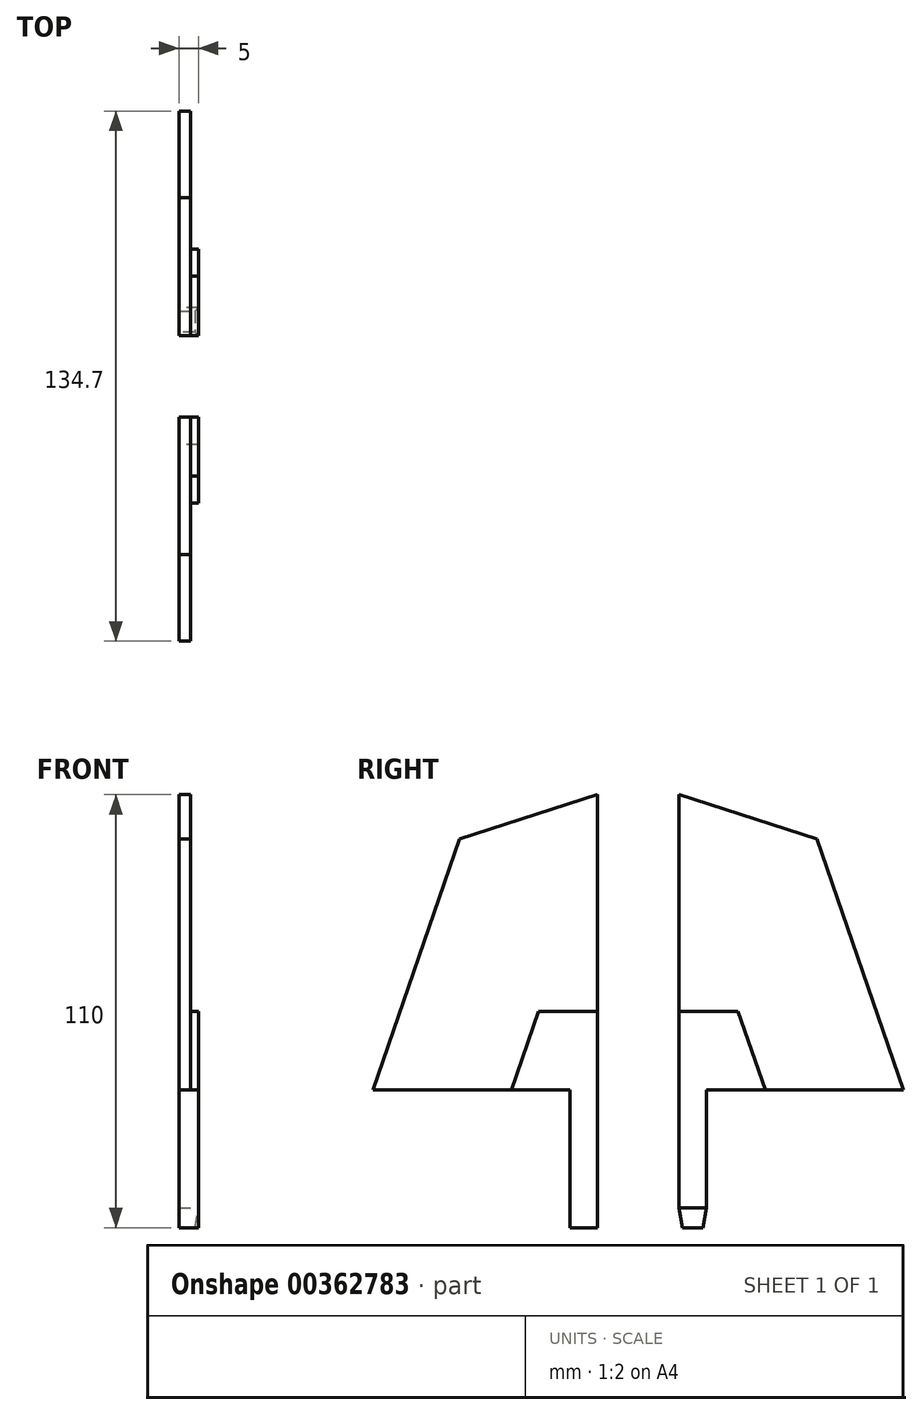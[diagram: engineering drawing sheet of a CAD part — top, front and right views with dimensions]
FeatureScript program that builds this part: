
annotation { "Feature Type Name" : "Feature", "Feature Type Description" : "" }
export const myFeature = defineFeature(function(context is Context, id is Id, definition is map)
    precondition{}
    {
        {
            var Q0;
            Q0=qCreatedBy(makeId("Right.planeOp"),FACE);
            var sketch = newSketch(context, id + "F0", { "sketchPlane" : qUnion([Q0])});
            skLineSegment(sketch, "E0", {"start": v(-17.35, -44.8) * mm, "end": v(-10.35, -44.8) * mm});
            skLineSegment(sketch, "E1", {"start": v(-10.35, -44.8) * mm, "end": v(-10.35, 65.2) * mm});
            skLineSegment(sketch, "E2", {"start": v(-17.35, -44.8) * mm, "end": v(-17.35, -9.8) * mm});
            skLineSegment(sketch, "E3", {"start": v(-17.35, -9.8) * mm, "end": v(-67.35, -9.8) * mm});
            skLineSegment(sketch, "E4", {"start": v(-10.35, 65.2) * mm, "end": v(-45.35, 53.94) * mm});
            skLineSegment(sketch, "E5", {"start": v(-45.35, 53.94) * mm, "end": v(-67.35, -9.8) * mm});
            skLineSegment(sketch, "E6.MirrorCS", {"start": v(10.35, -44.8) * mm, "end": v(10.35, 65.2) * mm});
            skLineSegment(sketch, "E7.MirrorCS", {"start": v(17.35, -44.8) * mm, "end": v(10.35, -44.8) * mm});
            skLineSegment(sketch, "E8.MirrorCS", {"start": v(17.35, -44.8) * mm, "end": v(17.35, -9.8) * mm});
            skLineSegment(sketch, "E9.MirrorCS", {"start": v(17.35, -9.8) * mm, "end": v(67.35, -9.8) * mm});
            skLineSegment(sketch, "E10.MirrorCS", {"start": v(45.35, 53.94) * mm, "end": v(67.35, -9.8) * mm});
            skLineSegment(sketch, "E11.MirrorCS", {"start": v(10.35, 65.2) * mm, "end": v(45.35, 53.94) * mm});
            skLineSegment(sketch, "E12", {"start": v(-10.35, 10.2) * mm, "end": v(-25.35, 10.2) * mm});
            skLineSegment(sketch, "E13", {"start": v(-25.35, 10.2) * mm, "end": v(-32.26, -9.8) * mm});
            skLineSegment(sketch, "E14.MirrorCS", {"start": v(10.35, 10.2) * mm, "end": v(25.35, 10.2) * mm});
            skLineSegment(sketch, "E15.MirrorCS", {"start": v(25.35, 10.2) * mm, "end": v(32.26, -9.8) * mm});
            skSolve(sketch);
        }
        {
            var Q0;
            {var subQ4=sQuery(id+"F0.wireOp",EDGE,"E0");Q0=makeQuery(id+"F0.imprint","IMPRINT",FACE,{"disambiguationData":[TD([[makeQuery(id+"F0.imprint","IMPRINT",EDGE,{"derivedFrom":subQ4}),1.0]])]});}
            extrude(context, id + "F1", {"entities" : qUnion([Q0]), "depth" : 5 * mm});
        }
        {
            var Q0;
            {var subQ0=sQuery(id+"F0.wireOp",EDGE,"E4");Q0=makeQuery(id+"F0.imprint","IMPRINT",FACE,{"disambiguationData":[TD([[makeQuery(id+"F0.imprint","IMPRINT",EDGE,{"derivedFrom":subQ0}),1.0]])]});}
            extrude(context, id + "F2", {"entities" : qUnion([Q0]), "operationType" : NewBodyOperationType.ADD, "depth" : 3 * mm});
        }
        {
            var Q0;
            {var subQ3=sQuery(id+"F0.wireOp",EDGE,"E7.MirrorCS");Q0=makeQuery(id+"F0.imprint","IMPRINT",FACE,{"disambiguationData":[TD([[makeQuery(id+"F0.imprint","IMPRINT",EDGE,{"derivedFrom":subQ3}),-1.0]])]});}
            extrude(context, id + "F3", {"entities" : qUnion([Q0]), "depth" : 5 * mm});
        }
        {
            var Q0;
            {var subQ1=sQuery(id+"F0.wireOp",EDGE,"E10.MirrorCS");Q0=makeQuery(id+"F0.imprint","IMPRINT",FACE,{"disambiguationData":[TD([[makeQuery(id+"F0.imprint","IMPRINT",EDGE,{"derivedFrom":subQ1}),-1.0]])]});}
            extrude(context, id + "F4", {"entities" : qUnion([Q0]), "operationType" : NewBodyOperationType.ADD, "depth" : 3 * mm});
        }
        {
            var Q0;
            Q0=makeQuery(id+"F3.opExtrude","SWEPT_EDGE",EDGE,{"disambiguationData":[OSD([sQuery(id+"F0.wireOp",EDGE,"E7.MirrorCS"),sQuery(id+"F0.wireOp",EDGE,"E8.MirrorCS")])]});
            var Q1;
            Q1=makeQuery(id+"F3.opExtrude","CAP_EDGE",EDGE,{"disambiguationData":[OSD([sQuery(id+"F0.wireOp",EDGE,"E7.MirrorCS")])],"isStart":false});
            var Q2;
            Q2=makeQuery(id+"F3.opExtrude","SWEPT_EDGE",EDGE,{"disambiguationData":[OSD([sQuery(id+"F0.wireOp",EDGE,"E6.MirrorCS"),sQuery(id+"F0.wireOp",EDGE,"E7.MirrorCS")])]});
            chamfer(context, id + "F5", {"entities" : qUnion([Q0, Q1, Q2]), "chamferType" : ChamferType.OFFSET_ANGLE, "width" : 5 * mm, "oppositeDirection" : false, "angle" : 10 * degree, "tangentPropagation" : true});
        }
    });
